# Revit family: Faucet-Wall_Mount-Lavatory-KOHLER-MODERN-K-97358T_1
name_source: partatom
category: Plumbing Fixtures
revit_build: Autodesk Revit 2017 (Build: 20160225_1515(x64)
units: mm (PartAtom-declared; Revit-internal decimal feet)

## family parameters
Cut with Voids When Loaded = No
Host = Face
OmniClass Number = 23.31.11.00
OmniClass Title = Faucets
Part Type = Normal
Room Calculation Point = No
Round Connector Dimension = Use Diameter
Shared = No

## types (4) — shared parameters
ADA Compliant = No
Assembly Code = D2010
CW Connection = Yes
Cold Water Inlet = Cold Water Inlet
Date Modified = 05/26/2020
Default Elevation = 36"
Description = Single Wall Outlet Faucet
Flow Rate = 0 GPM
HW Connection = Yes
Handle Clearance = 2 3/4"
Height = 2 5/16"
Hot Water Inlet = Hot Water Inlet
Length = 8 1/4"
Manufacturer = KOHLER Co.
Master Format 2014 = 22 41 39
Master Format 2014 Name = Residential Faucets, Supplies, and Trim
Material = Premium Metal Construction
Pressure = 0.00 psi
Product Name = MODERN
Spout Reach = 8 1/4"
URL = http://www.kohler.com.cn
Vent Connection = No
Waste Connection = No
Waste Water Outlet = Waste Water Outlet
WaterSense Certified = No
Width = 6 1/4"

## per-type parameters (varying)
| type | Drain Included | Finish | Model | Product Documentation Link | Product Page URL | Type |
| TT-Vibrant Titanium | Yes | Kohler-Metal-TT-Vibrant_Titanium | K-97358T-4-TT | http://files.kohler.com.cn | http://www.kohler.com.cn | 2 |
| Without Drain,CP-Polished Chrome | No | Kohler-Metal-CP-Polished_Chrome | K-97358T-4ND-CP |  |  | 3 |
| Without Drain,TT-Vibrant Titanium | No | Kohler-Metal-TT-Vibrant_Titanium | K-97358T-4ND-TT |  |  | 4 |
| CP-Polished Chrome | Yes | Kohler-Metal-CP-Polished_Chrome | K-97358T-4-CP | http://files.kohler.com.cn | http://www.kohler.com.cn | 1 |

## geometry (parser evidence)
native form markers: Sweep x4
no freeform markers — native parametric forms only
